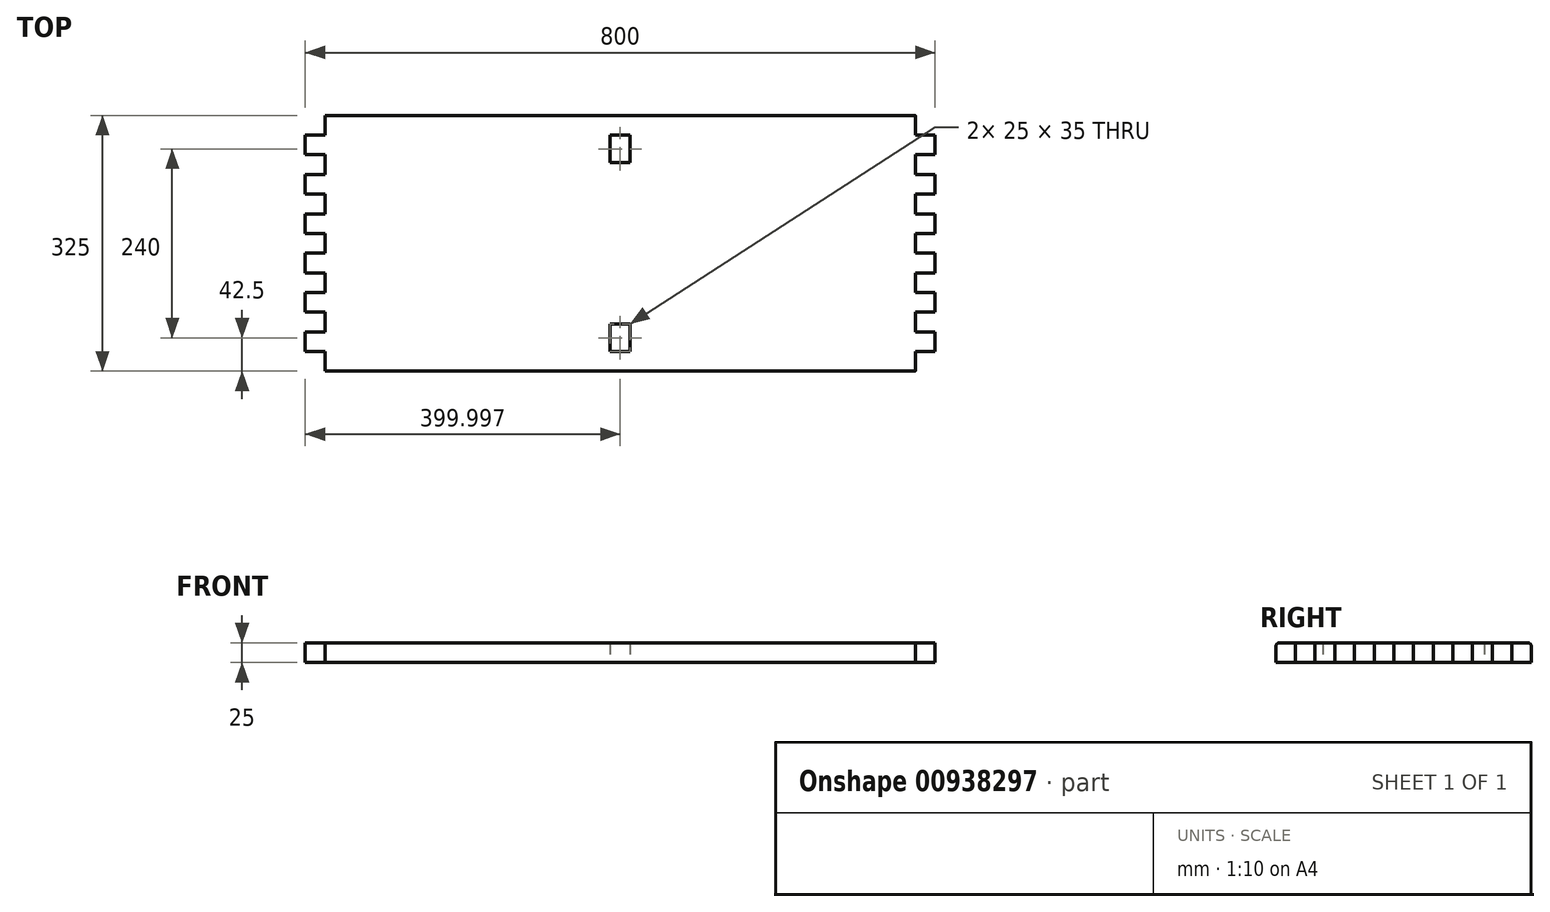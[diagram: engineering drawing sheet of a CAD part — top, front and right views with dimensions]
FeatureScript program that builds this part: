
annotation { "Feature Type Name" : "Feature", "Feature Type Description" : "" }
export const myFeature = defineFeature(function(context is Context, id is Id, definition is map)
    precondition{}
    {
        {
            var Q0;
            Q0=qCreatedBy(makeId("Top.planeOp"),FACE);
            var sketch = newSketch(context, id + "F0", { "sketchPlane" : qUnion([Q0])});
            skLineSegment(sketch, "E0.bottom", {"start": v(-297.66, 0) * mm, "end": v(77.34, 0) * mm});
            skLineSegment(sketch, "E0.top", {"start": v(-297.66, -325) * mm, "end": v(77.34, -325) * mm});
            skLineSegment(sketch, "E0.left", {"start": v(-297.66, 0) * mm, "end": v(-297.66, -325) * mm});
            skLineSegment(sketch, "E0.right", {"start": v(77.34, 0) * mm, "end": v(77.34, -325) * mm});
            skLineSegment(sketch, "E1.bottom", {"start": v(-297.66, -300) * mm, "end": v(-285.16, -300) * mm});
            skLineSegment(sketch, "E1.top", {"start": v(-297.66, -265) * mm, "end": v(-285.16, -265) * mm});
            skLineSegment(sketch, "E1.left", {"start": v(-297.66, -300) * mm, "end": v(-297.66, -265) * mm});
            skLineSegment(sketch, "E1.right", {"start": v(-285.16, -300) * mm, "end": v(-285.16, -265) * mm});
            skLineSegment(sketch, "E2.bottom", {"start": v(-297.66, -60) * mm, "end": v(-285.16, -60) * mm});
            skLineSegment(sketch, "E2.top", {"start": v(-297.66, -25) * mm, "end": v(-285.16, -25) * mm});
            skLineSegment(sketch, "E2.left", {"start": v(-297.66, -60) * mm, "end": v(-297.66, -25) * mm});
            skLineSegment(sketch, "E2.right", {"start": v(-285.16, -60) * mm, "end": v(-285.16, -25) * mm});
            skLineSegment(sketch, "E3.bottom", {"start": v(77.34, -300) * mm, "end": v(102.34, -300) * mm});
            skLineSegment(sketch, "E3.top", {"start": v(77.34, -275) * mm, "end": v(102.34, -275) * mm});
            skLineSegment(sketch, "E3.left", {"start": v(77.34, -300) * mm, "end": v(77.34, -275) * mm});
            skLineSegment(sketch, "E3.right", {"start": v(102.34, -300) * mm, "end": v(102.34, -275) * mm});
            skLineSegment(sketch, "E4.bottom", {"start": v(77.34, -250) * mm, "end": v(102.34, -250) * mm});
            skLineSegment(sketch, "E4.top", {"start": v(77.34, -225) * mm, "end": v(102.34, -225) * mm});
            skLineSegment(sketch, "E4.left", {"start": v(77.34, -250) * mm, "end": v(77.34, -225) * mm});
            skLineSegment(sketch, "E4.right", {"start": v(102.34, -250) * mm, "end": v(102.34, -225) * mm});
            skLineSegment(sketch, "E5.bottom", {"start": v(77.34, -200) * mm, "end": v(102.34, -200) * mm});
            skLineSegment(sketch, "E5.top", {"start": v(77.34, -175) * mm, "end": v(102.34, -175) * mm});
            skLineSegment(sketch, "E5.left", {"start": v(77.34, -200) * mm, "end": v(77.34, -175) * mm});
            skLineSegment(sketch, "E5.right", {"start": v(102.34, -200) * mm, "end": v(102.34, -175) * mm});
            skLineSegment(sketch, "E6.bottom", {"start": v(77.34, -150) * mm, "end": v(102.34, -150) * mm});
            skLineSegment(sketch, "E6.top", {"start": v(77.34, -125) * mm, "end": v(102.34, -125) * mm});
            skLineSegment(sketch, "E6.left", {"start": v(77.34, -150) * mm, "end": v(77.34, -125) * mm});
            skLineSegment(sketch, "E6.right", {"start": v(102.34, -150) * mm, "end": v(102.34, -125) * mm});
            skLineSegment(sketch, "E7.bottom", {"start": v(77.34, -100) * mm, "end": v(102.34, -100) * mm});
            skLineSegment(sketch, "E7.top", {"start": v(77.34, -75) * mm, "end": v(102.34, -75) * mm});
            skLineSegment(sketch, "E7.left", {"start": v(77.34, -100) * mm, "end": v(77.34, -75) * mm});
            skLineSegment(sketch, "E7.right", {"start": v(102.34, -100) * mm, "end": v(102.34, -75) * mm});
            skLineSegment(sketch, "E8.bottom", {"start": v(77.34, -50) * mm, "end": v(102.34, -50) * mm});
            skLineSegment(sketch, "E8.top", {"start": v(77.34, -25) * mm, "end": v(102.34, -25) * mm});
            skLineSegment(sketch, "E8.left", {"start": v(77.34, -50) * mm, "end": v(77.34, -25) * mm});
            skLineSegment(sketch, "E8.right", {"start": v(102.34, -50) * mm, "end": v(102.34, -25) * mm});
            skSolve(sketch);
        }
        {
            var Q0;
            {var subQ0=sQuery(id+"F0.wireOp",EDGE,"E3.bottom");Q0=makeQuery(id+"F0.imprint","IMPRINT",FACE,{"disambiguationData":[TD([[makeQuery(id+"F0.imprint","IMPRINT",EDGE,{"derivedFrom":subQ0}),1.0]])]});}
            var Q1;
            {var subQ0=sQuery(id+"F0.wireOp",EDGE,"E4.bottom");Q1=makeQuery(id+"F0.imprint","IMPRINT",FACE,{"disambiguationData":[TD([[makeQuery(id+"F0.imprint","IMPRINT",EDGE,{"derivedFrom":subQ0}),1.0]])]});}
            var Q2;
            {var subQ0=sQuery(id+"F0.wireOp",EDGE,"E5.bottom");Q2=makeQuery(id+"F0.imprint","IMPRINT",FACE,{"disambiguationData":[TD([[makeQuery(id+"F0.imprint","IMPRINT",EDGE,{"derivedFrom":subQ0}),1.0]])]});}
            var Q3;
            {var subQ0=sQuery(id+"F0.wireOp",EDGE,"E6.bottom");Q3=makeQuery(id+"F0.imprint","IMPRINT",FACE,{"disambiguationData":[TD([[makeQuery(id+"F0.imprint","IMPRINT",EDGE,{"derivedFrom":subQ0}),1.0]])]});}
            var Q4;
            {var subQ0=sQuery(id+"F0.wireOp",EDGE,"E7.bottom");Q4=makeQuery(id+"F0.imprint","IMPRINT",FACE,{"disambiguationData":[TD([[makeQuery(id+"F0.imprint","IMPRINT",EDGE,{"derivedFrom":subQ0}),1.0]])]});}
            var Q5;
            {var subQ2=sQuery(id+"F0.wireOp",EDGE,"E8.bottom");Q5=makeQuery(id+"F0.imprint","IMPRINT",FACE,{"disambiguationData":[TD([[makeQuery(id+"F0.imprint","IMPRINT",EDGE,{"derivedFrom":subQ2}),1.0]])]});}
            var Q6;
            {var subQ3=sQuery(id+"F0.wireOp",EDGE,"E0.bottom");Q6=makeQuery(id+"F0.imprint","IMPRINT",FACE,{"disambiguationData":[TD([[makeQuery(id+"F0.imprint","IMPRINT",EDGE,{"derivedFrom":subQ3}),-1.0]])]});}
            extrude(context, id + "F1", {"entities" : qUnion([Q0, Q1, Q2, Q3, Q4, Q5, Q6]), "depth" : 25 * mm, "offsetDistance" : 25 * mm});
        }
        {
            var Q0;
            Q0=makeQuery(id+"F1.opExtrude","SWEPT_BODY",BODY,{"disambiguationData":[OSD([sQuery(id+"F0.wireOp",EDGE,"E0.bottom"),sQuery(id+"F0.wireOp",EDGE,"E0.top"),sQuery(id+"F0.wireOp",EDGE,"E0.left"),sQuery(id+"F0.wireOp",EDGE,"E0.right"),sQuery(id+"F0.wireOp",EDGE,"E1.bottom"),sQuery(id+"F0.wireOp",EDGE,"E1.top"),sQuery(id+"F0.wireOp",EDGE,"E1.right"),sQuery(id+"F0.wireOp",EDGE,"E2.bottom"),sQuery(id+"F0.wireOp",EDGE,"E2.top"),sQuery(id+"F0.wireOp",EDGE,"E2.right"),sQuery(id+"F0.wireOp",EDGE,"E3.bottom"),sQuery(id+"F0.wireOp",EDGE,"E3.top"),sQuery(id+"F0.wireOp",EDGE,"E3.right"),sQuery(id+"F0.wireOp",EDGE,"E4.bottom"),sQuery(id+"F0.wireOp",EDGE,"E4.top"),sQuery(id+"F0.wireOp",EDGE,"E4.right"),sQuery(id+"F0.wireOp",EDGE,"E5.bottom"),sQuery(id+"F0.wireOp",EDGE,"E5.top"),sQuery(id+"F0.wireOp",EDGE,"E5.right"),sQuery(id+"F0.wireOp",EDGE,"E6.bottom"),sQuery(id+"F0.wireOp",EDGE,"E6.top"),sQuery(id+"F0.wireOp",EDGE,"E6.right"),sQuery(id+"F0.wireOp",EDGE,"E7.bottom"),sQuery(id+"F0.wireOp",EDGE,"E7.top"),sQuery(id+"F0.wireOp",EDGE,"E7.right"),sQuery(id+"F0.wireOp",EDGE,"E8.bottom"),sQuery(id+"F0.wireOp",EDGE,"E8.top"),sQuery(id+"F0.wireOp",EDGE,"E8.right")])]});
            var Q1;
            {var subQ0=sQuery(id+"F0.wireOp",EDGE,"E0.left");Q1=makeQuery(id+"F1.opExtrude","SWEPT_FACE",FACE,{"disambiguationData":[OSD([subQ0]),TDD([makeQuery(id+"F0.imprint","IMPRINT",EDGE,{"disambiguationData":[TD([[makeQuery(id+"F0.imprint","INTERSECT",VERTEX,{"derivedFrom":[subQ0,sQuery(id+"F0.wireOp",EDGE,"E2.bottom")]}),-1.0]])],"derivedFrom":subQ0})])]});}
            mirror(context, id + "F2", {"operationType" : NewBodyOperationType.ADD, "entities" : qUnion([Q0]), "mirrorPlane" : qUnion([Q1])});
        }
        {
            var Q0;
            {var subQ0=makeQuery(id+"F1.opExtrude","CAP_EDGE",EDGE,{"disambiguationData":[OSD([sQuery(id+"F0.wireOp",EDGE,"E0.bottom")])],"isStart":false});Q0=makeQuery(id+"F2.boolean.opBoolean","MERGE",EDGE,{"derivedFrom":[subQ0,makeQuery(id+"F2.opPattern","COPY",EDGE,{"derivedFrom":subQ0,"instanceName":"1"})]});}
            fillet(context, id + "F3", {"entities" : qUnion([Q0]), "radius" : 5 * mm, "tangentPropagation" : true, "allowEdgeOverflow" : false});
        }
        {
            var Q0;
            {var subQ0=makeQuery(id+"F1.opExtrude","CAP_EDGE",EDGE,{"disambiguationData":[OSD([sQuery(id+"F0.wireOp",EDGE,"E0.top")])],"isStart":false});Q0=makeQuery(id+"F2.boolean.opBoolean","MERGE",EDGE,{"derivedFrom":[subQ0,makeQuery(id+"F2.opPattern","COPY",EDGE,{"derivedFrom":subQ0,"instanceName":"1"})]});}
            fillet(context, id + "F4", {"entities" : qUnion([Q0]), "radius" : 5 * mm, "tangentPropagation" : true, "allowEdgeOverflow" : false});
        }
    });
